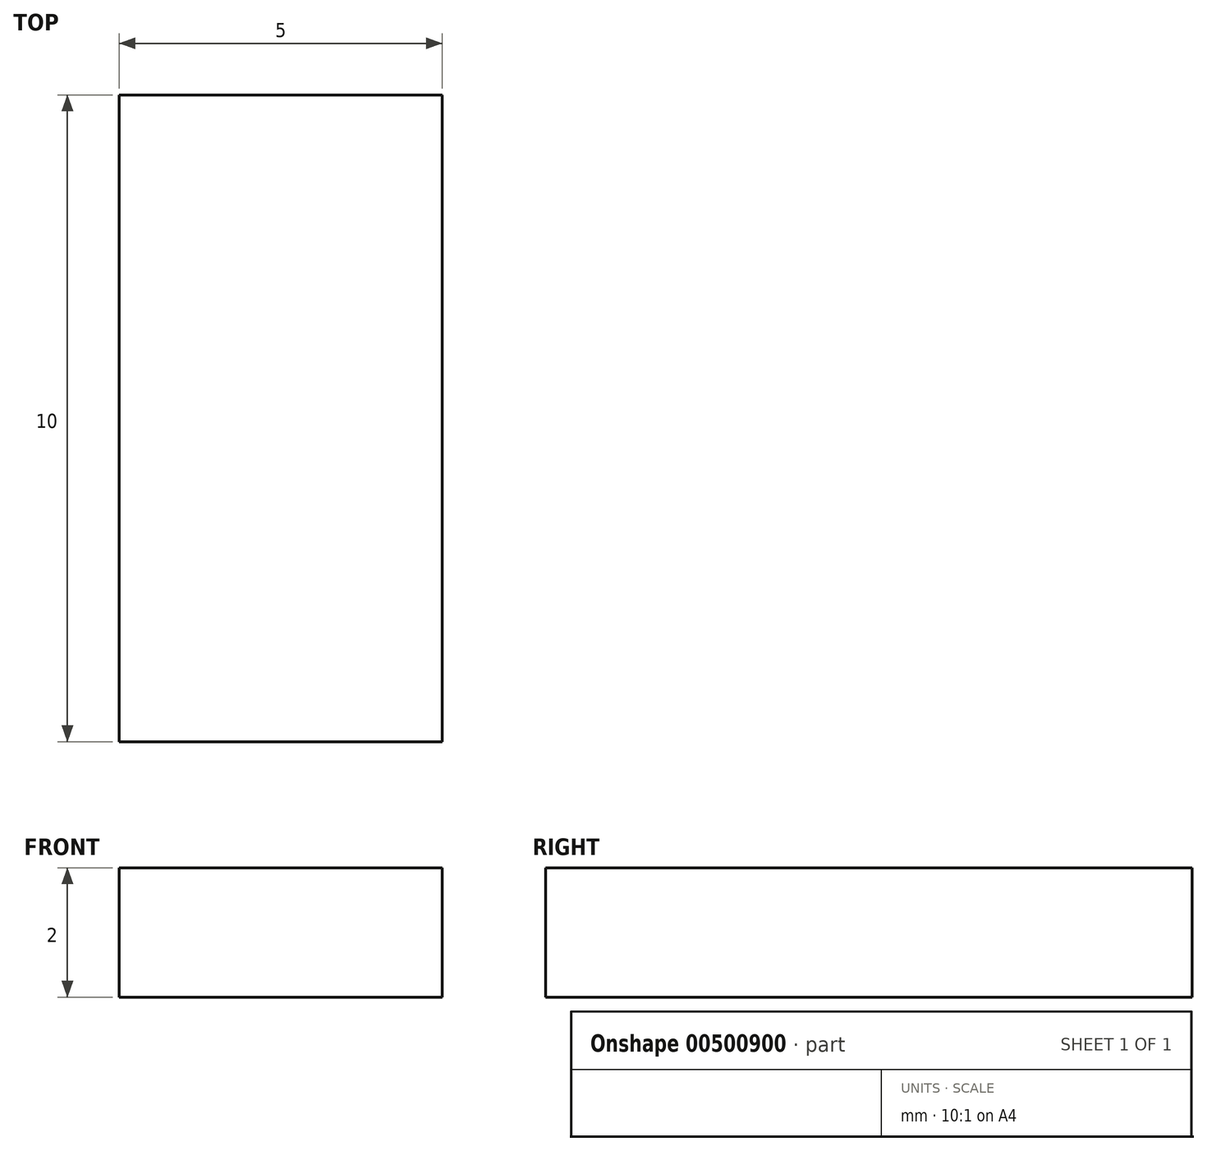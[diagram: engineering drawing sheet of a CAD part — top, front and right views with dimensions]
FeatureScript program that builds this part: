
annotation { "Feature Type Name" : "Feature", "Feature Type Description" : "" }
export const myFeature = defineFeature(function(context is Context, id is Id, definition is map)
    precondition{}
    {
        {
            var Q0;
            Q0=qCreatedBy(makeId("Top.planeOp"),FACE);
            var sketch = newSketch(context, id + "F0", { "sketchPlane" : qUnion([Q0])});
            skLineSegment(sketch, "E0.bottom", {"start": v(2.5, -5) * mm, "end": v(-2.5, -5) * mm});
            skLineSegment(sketch, "E0.top", {"start": v(2.5, 5) * mm, "end": v(-2.5, 5) * mm});
            skLineSegment(sketch, "E0.left", {"start": v(2.5, -5) * mm, "end": v(2.5, 5) * mm});
            skLineSegment(sketch, "E0.right", {"start": v(-2.5, -5) * mm, "end": v(-2.5, 5) * mm});
            skPoint(sketch, "E0.middle", {"position": v(0, 0) * mm});
            skSolve(sketch);
        }
        {
            var Q0;
            Q0=makeQuery(id+"F0.imprint","IMPRINT",FACE,{"disambiguationData":[TD([[makeQuery(id+"F0.imprint","IMPRINT",EDGE,{"derivedFrom":sQuery(id+"F0.wireOp",EDGE,"E0.bottom")}),-1.0]])]});
            extrude(context, id + "F1", {"entities" : qUnion([Q0]), "depth" : 2 * mm, "offsetDistance" : 25 * mm});
        }
    });
